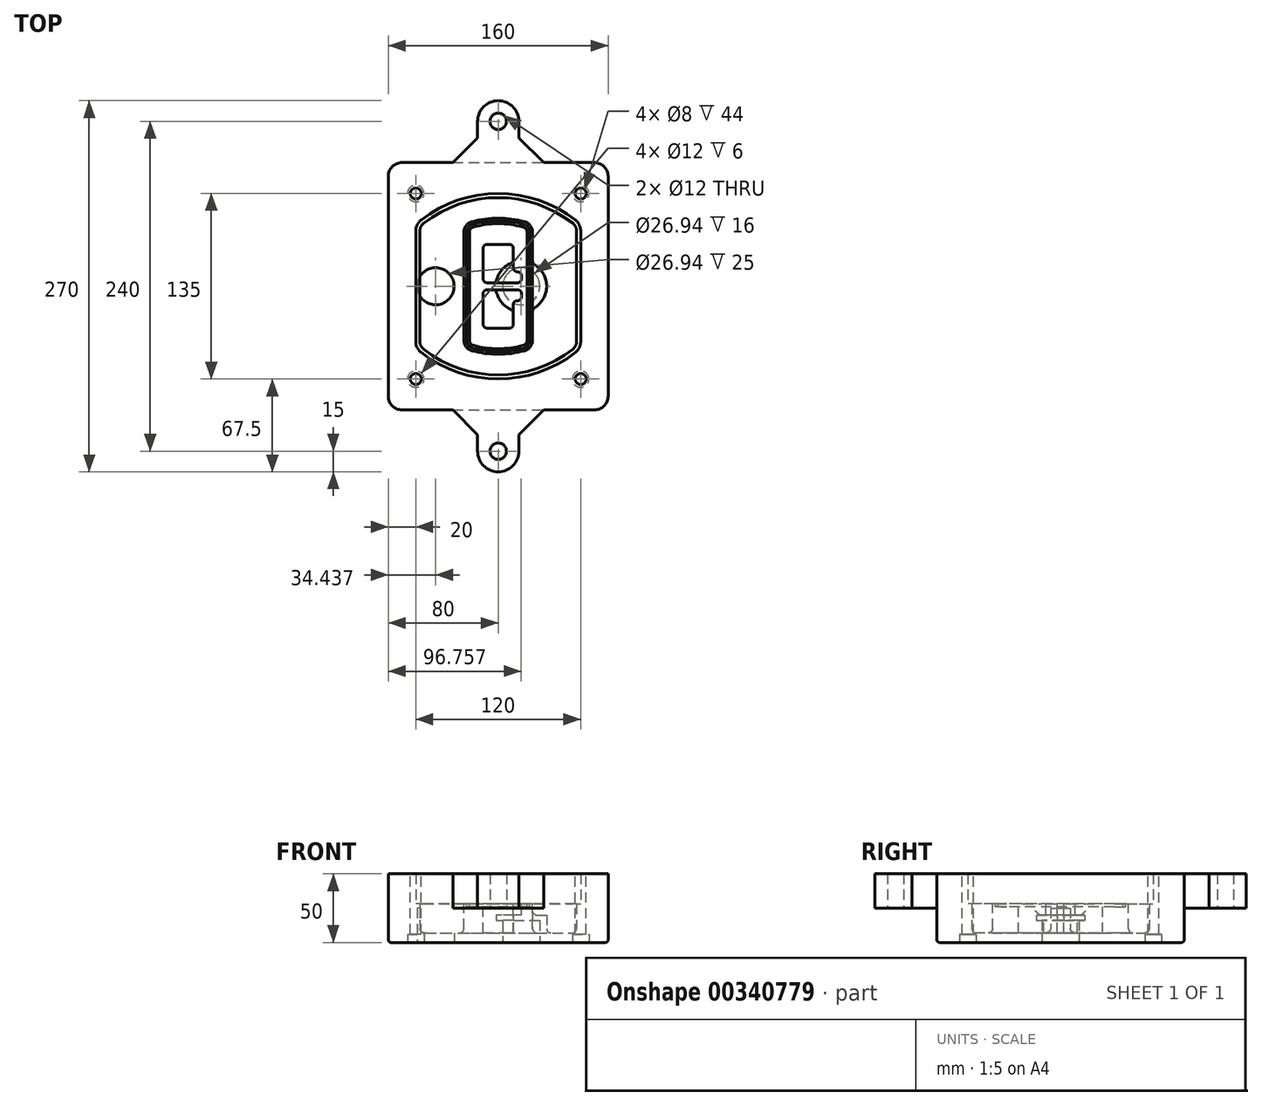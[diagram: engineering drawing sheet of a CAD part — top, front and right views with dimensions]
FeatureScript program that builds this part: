
annotation { "Feature Type Name" : "Feature", "Feature Type Description" : "" }
export const myFeature = defineFeature(function(context is Context, id is Id, definition is map)
    precondition{}
    {
        {
            var Q0;
            Q0=qCreatedBy(makeId("Top.planeOp"),FACE);
            var sketch = newSketch(context, id + "F0", { "sketchPlane" : qUnion([Q0])});
            skPoint(sketch, "E0.rect.middle", {"position": v(0, 0) * mm});
            skLineSegment(sketch, "E1.bottom", {"start": v(-70, -90) * mm, "end": v(70, -90) * mm});
            skLineSegment(sketch, "E1.top", {"start": v(-70, 90) * mm, "end": v(70, 90) * mm});
            skLineSegment(sketch, "E1.left", {"start": v(-80, -80) * mm, "end": v(-80, 80) * mm});
            skLineSegment(sketch, "E1.right", {"start": v(80, -80) * mm, "end": v(80, 80) * mm});
            skLineSegment(sketch, "E2", {"start": v(-80, 90) * mm, "end": v(80, -90) * mm, "construction": true});
            skLineSegment(sketch, "E3", {"start": v(80, 90) * mm, "end": v(-80, -90) * mm, "construction": true});
            skCircle(sketch, "E4", {"center": v(-60, 67.5) * mm, "radius": 4 * mm});
            skCircle(sketch, "E5", {"center": v(60, 67.5) * mm, "radius": 4 * mm});
            skCircle(sketch, "E6", {"center": v(60, -67.5) * mm, "radius": 4 * mm});
            skCircle(sketch, "E7", {"center": v(-60, -67.5) * mm, "radius": 4 * mm});
            skLineSegment(sketch, "E8", {"start": v(-60, 67.5) * mm, "end": v(60, 67.5) * mm, "construction": true});
            skLineSegment(sketch, "E9", {"start": v(60, 67.5) * mm, "end": v(60, -67.5) * mm, "construction": true});
            skLineSegment(sketch, "E10", {"start": v(60, -67.5) * mm, "end": v(-60, -67.5) * mm, "construction": true});
            skLineSegment(sketch, "E11", {"start": v(-60, -67.5) * mm, "end": v(-60, 67.5) * mm, "construction": true});
            skLineSegment(sketch, "E12", {"start": v(-60, 40.3) * mm, "end": v(-60, -40.3) * mm});
            skLineSegment(sketch, "E13", {"start": v(60, 40.3) * mm, "end": v(60, -40.3) * mm});
            skArc(sketch, "E14", {"start": v(56.15, 48.18) * mm, "mid": v(0, 67.5) * mm, "end": v(-56.15, 48.18) * mm});
            skArc(sketch, "E15", {"start": v(-56.15, -48.18) * mm, "mid": v(0, -67.5) * mm, "end": v(56.15, -48.18) * mm});
            skLineSegment(sketch, "E16", {"start": v(-60, 0) * mm, "end": v(60, 0) * mm, "construction": true});
            skPoint(sketch, "E17.visualSharp", {"position": v(-60, -45) * mm});
            skArc(sketch, "E17.filletArc", {"start": v(-60, -40.3) * mm, "mid": v(-58.99, -44.68) * mm, "end": v(-56.15, -48.18) * mm});
            skPoint(sketch, "E18.visualSharp", {"position": v(-60, 45) * mm});
            skArc(sketch, "E18.filletArc", {"start": v(-56.15, 48.18) * mm, "mid": v(-58.99, 44.68) * mm, "end": v(-60, 40.3) * mm});
            skPoint(sketch, "E19.visualSharp", {"position": v(60, 45) * mm});
            skArc(sketch, "E19.filletArc", {"start": v(60, 40.3) * mm, "mid": v(58.99, 44.68) * mm, "end": v(56.15, 48.18) * mm});
            skPoint(sketch, "E20.visualSharp", {"position": v(60, -45) * mm});
            skArc(sketch, "E20.filletArc", {"start": v(56.15, -48.18) * mm, "mid": v(58.99, -44.68) * mm, "end": v(60, -40.3) * mm});
            skPoint(sketch, "E21.visualSharp", {"position": v(-80, 90) * mm});
            skArc(sketch, "E21.filletArc", {"start": v(-70, 90) * mm, "mid": v(-77.07, 87.07) * mm, "end": v(-80, 80) * mm});
            skPoint(sketch, "E22.visualSharp", {"position": v(80, 90) * mm});
            skArc(sketch, "E22.filletArc", {"start": v(80, 80) * mm, "mid": v(77.07, 87.07) * mm, "end": v(70, 90) * mm});
            skPoint(sketch, "E23.visualSharp", {"position": v(80, -90) * mm});
            skArc(sketch, "E23.filletArc", {"start": v(70, -90) * mm, "mid": v(77.07, -87.07) * mm, "end": v(80, -80) * mm});
            skPoint(sketch, "E24.visualSharp", {"position": v(-80, -90) * mm});
            skArc(sketch, "E24.filletArc", {"start": v(-80, -80) * mm, "mid": v(-77.07, -87.07) * mm, "end": v(-70, -90) * mm});
            skArc(sketch, "E25.0", {"start": v(57, 40.3) * mm, "mid": v(56.3, 43.36) * mm, "end": v(54.3, 45.81) * mm});
            skLineSegment(sketch, "E25.1", {"start": v(57, 40.3) * mm, "end": v(57, -40.3) * mm});
            skArc(sketch, "E25.2", {"start": v(54.3, -45.81) * mm, "mid": v(56.3, -43.36) * mm, "end": v(57, -40.3) * mm});
            skArc(sketch, "E25.3", {"start": v(-54.3, -45.81) * mm, "mid": v(0, -64.5) * mm, "end": v(54.3, -45.81) * mm});
            skArc(sketch, "E25.4", {"start": v(-57, -40.3) * mm, "mid": v(-56.3, -43.36) * mm, "end": v(-54.3, -45.81) * mm});
            skArc(sketch, "E25.5", {"start": v(54.3, 45.81) * mm, "mid": v(0, 64.5) * mm, "end": v(-54.3, 45.81) * mm});
            skLineSegment(sketch, "E25.6", {"start": v(-57, 40.3) * mm, "end": v(-57, -40.3) * mm});
            skArc(sketch, "E25.7", {"start": v(-54.3, 45.81) * mm, "mid": v(-56.3, 43.36) * mm, "end": v(-57, 40.3) * mm});
            skArc(sketch, "E26.0", {"start": v(-58.62, 51.33) * mm, "mid": v(-62.58, 46.43) * mm, "end": v(-64, 40.3) * mm});
            skArc(sketch, "E26.1", {"start": v(58.62, 51.33) * mm, "mid": v(0, 71.5) * mm, "end": v(-58.62, 51.33) * mm});
            skArc(sketch, "E26.2", {"start": v(64, 40.3) * mm, "mid": v(62.58, 46.43) * mm, "end": v(58.62, 51.33) * mm});
            skLineSegment(sketch, "E26.3", {"start": v(64, 40.3) * mm, "end": v(64, -40.3) * mm});
            skArc(sketch, "E26.4", {"start": v(58.62, -51.33) * mm, "mid": v(62.58, -46.43) * mm, "end": v(64, -40.3) * mm});
            skLineSegment(sketch, "E26.5", {"start": v(-64, 40.3) * mm, "end": v(-64, -40.3) * mm});
            skArc(sketch, "E26.6", {"start": v(-58.62, -51.33) * mm, "mid": v(0, -71.5) * mm, "end": v(58.62, -51.33) * mm});
            skArc(sketch, "E26.7", {"start": v(-64, -40.3) * mm, "mid": v(-62.58, -46.43) * mm, "end": v(-58.62, -51.33) * mm});
            skSolve(sketch);
        }
        {
            var Q0;
            Q0=makeQuery(id+"F0.imprint","IMPRINT",FACE,{"disambiguationData":[TD([[makeQuery(id+"F0.imprint","IMPRINT",EDGE,{"derivedFrom":sQuery(id+"F0.wireOp",EDGE,"E1.bottom")}),1.0]])]});
            var Q1;
            Q1=makeQuery(id+"F0.imprint","IMPRINT",FACE,{"disambiguationData":[TD([[makeQuery(id+"F0.imprint","IMPRINT",EDGE,{"derivedFrom":sQuery(id+"F0.wireOp",EDGE,"E12")}),1.0]])]});
            var Q2;
            Q2=makeQuery(id+"F0.imprint","IMPRINT",FACE,{"disambiguationData":[TD([[makeQuery(id+"F0.imprint","IMPRINT",EDGE,{"derivedFrom":sQuery(id+"F0.wireOp",EDGE,"E25.0")}),1.0]])]});
            var Q3;
            Q3=makeQuery(id+"F0.imprint","IMPRINT",FACE,{"disambiguationData":[TD([[makeQuery(id+"F0.imprint","IMPRINT",EDGE,{"derivedFrom":sQuery(id+"F0.wireOp",EDGE,"E12")}),-1.0]])]});
            extrude(context, id + "F1", {"entities" : qUnion([Q0, Q1, Q2, Q3]), "oppositeDirection" : true, "depth" : 25 * mm});
        }
        {
            var Q0;
            Q0=makeQuery(id+"F0.imprint","IMPRINT",FACE,{"disambiguationData":[TD([[makeQuery(id+"F0.imprint","IMPRINT",EDGE,{"derivedFrom":sQuery(id+"F0.wireOp",EDGE,"E12")}),1.0]])]});
            extrude(context, id + "F2", {"entities" : qUnion([Q0]), "operationType" : NewBodyOperationType.ADD, "depth" : 3 * mm});
        }
        {
            var Q0;
            Q0=makeQuery(id+"F0.imprint","IMPRINT",FACE,{"disambiguationData":[TD([[makeQuery(id+"F0.imprint","IMPRINT",EDGE,{"derivedFrom":sQuery(id+"F0.wireOp",EDGE,"E25.0")}),1.0]])]});
            extrude(context, id + "F3", {"entities" : qUnion([Q0]), "operationType" : NewBodyOperationType.REMOVE, "oppositeDirection" : true, "depth" : 18 * mm});
        }
        {
            var Q0;
            Q0=makeQuery(id+"F2.opExtrude","CAP_FACE",FACE,{"disambiguationData":[OSD([sQuery(id+"F0.wireOp",EDGE,"E12"),sQuery(id+"F0.wireOp",EDGE,"E13"),sQuery(id+"F0.wireOp",EDGE,"E14"),sQuery(id+"F0.wireOp",EDGE,"E15"),sQuery(id+"F0.wireOp",EDGE,"E17.filletArc"),sQuery(id+"F0.wireOp",EDGE,"E18.filletArc"),sQuery(id+"F0.wireOp",EDGE,"E19.filletArc"),sQuery(id+"F0.wireOp",EDGE,"E20.filletArc"),sQuery(id+"F0.wireOp",EDGE,"E25.0"),sQuery(id+"F0.wireOp",EDGE,"E25.1"),sQuery(id+"F0.wireOp",EDGE,"E25.2"),sQuery(id+"F0.wireOp",EDGE,"E25.3"),sQuery(id+"F0.wireOp",EDGE,"E25.4"),sQuery(id+"F0.wireOp",EDGE,"E25.5"),sQuery(id+"F0.wireOp",EDGE,"E25.6"),sQuery(id+"F0.wireOp",EDGE,"E25.7")])],"isStart":false});
            var sketch = newSketch(context, id + "F4", { "sketchPlane" : qUnion([Q0])});
            skArc(sketch, "E27.0", {"start": v(-19.08, -46.97) * mm, "mid": v(0, -49.5) * mm, "end": v(19.08, -46.97) * mm});
            skArc(sketch, "E28.0", {"start": v(19.08, 46.97) * mm, "mid": v(0, 49.5) * mm, "end": v(-19.08, 46.97) * mm});
            skLineSegment(sketch, "E29", {"start": v(-25, 39.25) * mm, "end": v(-25, -39.25) * mm});
            skLineSegment(sketch, "E30", {"start": v(25, 39.25) * mm, "end": v(25, -39.25) * mm});
            skLineSegment(sketch, "E31", {"start": v(-25, 45.1) * mm, "end": v(25, 45.1) * mm, "construction": true});
            skLineSegment(sketch, "E32", {"start": v(-25, -45.1) * mm, "end": v(25, -45.1) * mm, "construction": true});
            skPoint(sketch, "E33.visualSharp", {"position": v(-25, 45.1) * mm});
            skArc(sketch, "E33.filletArc", {"start": v(-19.08, 46.97) * mm, "mid": v(-23.35, 44.11) * mm, "end": v(-25, 39.25) * mm});
            skPoint(sketch, "E34.visualSharp", {"position": v(25, 45.1) * mm});
            skArc(sketch, "E34.filletArc", {"start": v(25, 39.25) * mm, "mid": v(23.35, 44.11) * mm, "end": v(19.08, 46.97) * mm});
            skPoint(sketch, "E35.visualSharp", {"position": v(25, -45.1) * mm});
            skArc(sketch, "E35.filletArc", {"start": v(19.08, -46.97) * mm, "mid": v(23.35, -44.11) * mm, "end": v(25, -39.25) * mm});
            skPoint(sketch, "E36.visualSharp", {"position": v(-25, -45.1) * mm});
            skArc(sketch, "E36.filletArc", {"start": v(-25, -39.25) * mm, "mid": v(-23.35, -44.11) * mm, "end": v(-19.08, -46.97) * mm});
            skArc(sketch, "E37.0", {"start": v(54.3, 45.81) * mm, "mid": v(0, 64.5) * mm, "end": v(-54.3, 45.81) * mm});
            skArc(sketch, "E37.1", {"start": v(-54.3, 45.81) * mm, "mid": v(-56.3, 43.36) * mm, "end": v(-57, 40.3) * mm});
            skLineSegment(sketch, "E37.2", {"start": v(-57, 40.3) * mm, "end": v(-57, -40.3) * mm});
            skArc(sketch, "E37.3", {"start": v(-57, -40.3) * mm, "mid": v(-56.3, -43.36) * mm, "end": v(-54.3, -45.81) * mm});
            skArc(sketch, "E37.4", {"start": v(-54.3, -45.81) * mm, "mid": v(0, -64.5) * mm, "end": v(54.3, -45.81) * mm});
            skArc(sketch, "E37.5", {"start": v(54.3, -45.81) * mm, "mid": v(56.3, -43.36) * mm, "end": v(57, -40.3) * mm});
            skLineSegment(sketch, "E37.6", {"start": v(57, 40.3) * mm, "end": v(57, -40.3) * mm});
            skArc(sketch, "E37.7", {"start": v(57, 40.3) * mm, "mid": v(56.3, 43.36) * mm, "end": v(54.3, 45.81) * mm});
            skLineSegment(sketch, "E38.0", {"start": v(23, 39.25) * mm, "end": v(23, -39.25) * mm});
            skArc(sketch, "E38.1", {"start": v(18.56, -45.04) * mm, "mid": v(21.76, -42.9) * mm, "end": v(23, -39.25) * mm});
            skArc(sketch, "E38.2", {"start": v(-18.56, -45.04) * mm, "mid": v(0, -47.5) * mm, "end": v(18.56, -45.04) * mm});
            skArc(sketch, "E38.3", {"start": v(-23, -39.25) * mm, "mid": v(-21.76, -42.9) * mm, "end": v(-18.56, -45.04) * mm});
            skLineSegment(sketch, "E38.4", {"start": v(-23, 39.25) * mm, "end": v(-23, -39.25) * mm});
            skArc(sketch, "E38.5", {"start": v(23, 39.25) * mm, "mid": v(21.76, 42.9) * mm, "end": v(18.56, 45.04) * mm});
            skArc(sketch, "E38.6", {"start": v(-18.56, 45.04) * mm, "mid": v(-21.76, 42.9) * mm, "end": v(-23, 39.25) * mm});
            skArc(sketch, "E38.7", {"start": v(18.56, 45.04) * mm, "mid": v(0, 47.5) * mm, "end": v(-18.56, 45.04) * mm});
            skArc(sketch, "E39.0", {"start": v(21, 39.25) * mm, "mid": v(20.18, 41.68) * mm, "end": v(18.04, 43.1) * mm});
            skLineSegment(sketch, "E39.1", {"start": v(21, 39.25) * mm, "end": v(21, -39.25) * mm});
            skArc(sketch, "E39.2", {"start": v(18.04, -43.1) * mm, "mid": v(20.18, -41.68) * mm, "end": v(21, -39.25) * mm});
            skArc(sketch, "E39.3", {"start": v(-18.04, -43.1) * mm, "mid": v(0, -45.5) * mm, "end": v(18.04, -43.1) * mm});
            skArc(sketch, "E39.4", {"start": v(-21, -39.25) * mm, "mid": v(-20.18, -41.68) * mm, "end": v(-18.04, -43.1) * mm});
            skArc(sketch, "E39.5", {"start": v(18.04, 43.1) * mm, "mid": v(0, 45.5) * mm, "end": v(-18.04, 43.1) * mm});
            skLineSegment(sketch, "E39.6", {"start": v(-21, 39.25) * mm, "end": v(-21, -39.25) * mm});
            skArc(sketch, "E39.7", {"start": v(-18.04, 43.1) * mm, "mid": v(-20.18, 41.68) * mm, "end": v(-21, 39.25) * mm});
            skLineSegment(sketch, "E40", {"start": v(-25, 0) * mm, "end": v(25, 0) * mm, "construction": true});
            skLineSegment(sketch, "E41", {"start": v(-11, 5.5) * mm, "end": v(-11, 27.5) * mm});
            skLineSegment(sketch, "E42", {"start": v(-8, 30.5) * mm, "end": v(8, 30.5) * mm});
            skLineSegment(sketch, "E43", {"start": v(11, 27.5) * mm, "end": v(11, 13.5) * mm});
            skLineSegment(sketch, "E44", {"start": v(14, 10.5) * mm, "end": v(14, 10.5) * mm});
            skLineSegment(sketch, "E45", {"start": v(17, 7.5) * mm, "end": v(17, 5.5) * mm});
            skLineSegment(sketch, "E46", {"start": v(14, 2.5) * mm, "end": v(-8, 2.5) * mm});
            skPoint(sketch, "E47.visualSharp", {"position": v(-11, 30.5) * mm});
            skArc(sketch, "E47.filletArc", {"start": v(-8, 30.5) * mm, "mid": v(-10.12, 29.62) * mm, "end": v(-11, 27.5) * mm});
            skPoint(sketch, "E48.visualSharp", {"position": v(11, 30.5) * mm});
            skArc(sketch, "E48.filletArc", {"start": v(11, 27.5) * mm, "mid": v(10.12, 29.62) * mm, "end": v(8, 30.5) * mm});
            skPoint(sketch, "E49.visualSharp", {"position": v(11, 10.5) * mm});
            skArc(sketch, "E49.filletArc", {"start": v(11, 13.5) * mm, "mid": v(11.88, 11.38) * mm, "end": v(14, 10.5) * mm});
            skPoint(sketch, "E50.visualSharp", {"position": v(17, 10.5) * mm});
            skArc(sketch, "E50.filletArc", {"start": v(17, 7.5) * mm, "mid": v(16.12, 9.62) * mm, "end": v(14, 10.5) * mm});
            skPoint(sketch, "E51.visualSharp", {"position": v(17, 2.5) * mm});
            skArc(sketch, "E51.filletArc", {"start": v(14, 2.5) * mm, "mid": v(16.12, 3.38) * mm, "end": v(17, 5.5) * mm});
            skPoint(sketch, "E52.visualSharp", {"position": v(-11, 2.5) * mm});
            skArc(sketch, "E52.filletArc", {"start": v(-11, 5.5) * mm, "mid": v(-10.12, 3.38) * mm, "end": v(-8, 2.5) * mm});
            skLineSegment(sketch, "E53.0.MirrorCS", {"start": v(14, -2.5) * mm, "end": v(-8, -2.5) * mm});
            skArc(sketch, "E54.0.MirrorCS", {"start": v(-11, -5.5) * mm, "mid": v(-10.12, -3.38) * mm, "end": v(-8, -2.5) * mm});
            skLineSegment(sketch, "E55.0.MirrorCS", {"start": v(-11, -5.5) * mm, "end": v(-11, -27.5) * mm});
            skArc(sketch, "E56.0.MirrorCS", {"start": v(-8, -30.5) * mm, "mid": v(-10.12, -29.62) * mm, "end": v(-11, -27.5) * mm});
            skLineSegment(sketch, "E57.0.MirrorCS", {"start": v(-8, -30.5) * mm, "end": v(8, -30.5) * mm});
            skArc(sketch, "E58.0.MirrorCS", {"start": v(11, -27.5) * mm, "mid": v(10.12, -29.62) * mm, "end": v(8, -30.5) * mm});
            skLineSegment(sketch, "E59.0.MirrorCS", {"start": v(11, -27.5) * mm, "end": v(11, -13.5) * mm});
            skArc(sketch, "E60.0.MirrorCS", {"start": v(11, -13.5) * mm, "mid": v(11.88, -11.38) * mm, "end": v(14, -10.5) * mm});
            skArc(sketch, "E61.0.MirrorCS", {"start": v(17, -7.5) * mm, "mid": v(16.12, -9.62) * mm, "end": v(14, -10.5) * mm});
            skLineSegment(sketch, "E62.0.MirrorCS", {"start": v(17, -7.5) * mm, "end": v(17, -5.5) * mm});
            skArc(sketch, "E63.0.MirrorCS", {"start": v(14, -2.5) * mm, "mid": v(16.12, -3.38) * mm, "end": v(17, -5.5) * mm});
            skSolve(sketch);
        }
        {
            var Q0;
            Q0=makeQuery(id+"F4.imprint","IMPRINT",FACE,{"disambiguationData":[TD([[makeQuery(id+"F4.imprint","IMPRINT",EDGE,{"derivedFrom":sQuery(id+"F4.wireOp",EDGE,"E27.0")}),1.0]])]});
            var Q1;
            Q1=makeQuery(id+"F4.imprint","IMPRINT",FACE,{"disambiguationData":[TD([[makeQuery(id+"F4.imprint","IMPRINT",EDGE,{"derivedFrom":sQuery(id+"F4.wireOp",EDGE,"E38.0")}),-1.0]])]});
            var Q2;
            Q2=makeQuery(id+"F4.imprint","IMPRINT",FACE,{"disambiguationData":[TD([[makeQuery(id+"F4.imprint","IMPRINT",EDGE,{"derivedFrom":sQuery(id+"F4.wireOp",EDGE,"E39.0")}),1.0]])]});
            extrude(context, id + "F5", {"entities" : qUnion([Q0, Q1, Q2]), "operationType" : NewBodyOperationType.ADD, "endBound" : BoundingType.UP_TO_NEXT, "oppositeDirection" : true, "depth" : 25 * mm});
        }
        {
            var Q0;
            Q0=makeQuery(id+"F4.imprint","IMPRINT",FACE,{"disambiguationData":[TD([[makeQuery(id+"F4.imprint","IMPRINT",EDGE,{"derivedFrom":sQuery(id+"F4.wireOp",EDGE,"E38.0")}),-1.0]])]});
            extrude(context, id + "F6", {"entities" : qUnion([Q0]), "operationType" : NewBodyOperationType.REMOVE, "oppositeDirection" : true, "depth" : 2 * mm});
        }
        {
            var Q0;
            Q0=makeQuery(id+"F1.opExtrude","CAP_FACE",FACE,{"disambiguationData":[OSD([sQuery(id+"F0.wireOp",EDGE,"E1.bottom"),sQuery(id+"F0.wireOp",EDGE,"E1.top"),sQuery(id+"F0.wireOp",EDGE,"E1.left"),sQuery(id+"F0.wireOp",EDGE,"E1.right"),sQuery(id+"F0.wireOp",EDGE,"E4"),sQuery(id+"F0.wireOp",EDGE,"E5"),sQuery(id+"F0.wireOp",EDGE,"E6"),sQuery(id+"F0.wireOp",EDGE,"E7"),sQuery(id+"F0.wireOp",EDGE,"E21.filletArc"),sQuery(id+"F0.wireOp",EDGE,"E22.filletArc"),sQuery(id+"F0.wireOp",EDGE,"E23.filletArc"),sQuery(id+"F0.wireOp",EDGE,"E24.filletArc")])],"isStart":false});
            var sketch = newSketch(context, id + "F7", { "sketchPlane" : qUnion([Q0])});
            skCircle(sketch, "E64", {"center": v(16.76, 0) * mm, "radius": 13.47 * mm});
            skCircle(sketch, "E65", {"center": v(-45.56, 0) * mm, "radius": 13.47 * mm});
            skLineSegment(sketch, "E66", {"start": v(80, 0) * mm, "end": v(-80, 0) * mm});
            skCircle(sketch, "E67", {"center": v(16.76, 0) * mm, "radius": 18.47 * mm});
            skCircle(sketch, "E68", {"center": v(60, -67.5) * mm, "radius": 6 * mm});
            skCircle(sketch, "E69", {"center": v(-60, -67.5) * mm, "radius": 6 * mm});
            skCircle(sketch, "E70", {"center": v(-60, 67.5) * mm, "radius": 6 * mm});
            skCircle(sketch, "E71", {"center": v(60, 67.5) * mm, "radius": 6 * mm});
            skSolve(sketch);
        }
        {
            var Q0;
            {var subQ1=sQuery(id+"F7.wireOp",EDGE,"E66");var subQ4=sQuery(id+"F7.wireOp",EDGE,"E64");var subQ6=makeQuery(id+"F7.imprint","INTERSECT",VERTEX,{"disambiguationData":[OD(0.0)],"derivedFrom":[subQ4,subQ1]});Q0=makeQuery(id+"F7.imprint","IMPRINT",FACE,{"disambiguationData":[TD([[makeQuery(id+"F7.imprint","IMPRINT",EDGE,{"disambiguationData":[TD([[subQ6,-1.0]])],"derivedFrom":subQ4}),-1.0]])]});}
            var Q1;
            {var subQ0=sQuery(id+"F7.wireOp",EDGE,"E66");var subQ1=sQuery(id+"F7.wireOp",EDGE,"E64");var subQ3=makeQuery(id+"F7.imprint","INTERSECT",VERTEX,{"disambiguationData":[OD(0.0)],"derivedFrom":[subQ1,subQ0]});Q1=makeQuery(id+"F7.imprint","IMPRINT",FACE,{"disambiguationData":[TD([[makeQuery(id+"F7.imprint","IMPRINT",EDGE,{"disambiguationData":[TD([[subQ3,-1.0]])],"derivedFrom":subQ1}),1.0]])]});}
            var Q2;
            {var subQ0=sQuery(id+"F7.wireOp",EDGE,"E66");var subQ1=sQuery(id+"F7.wireOp",EDGE,"E64");var subQ3=makeQuery(id+"F7.imprint","INTERSECT",VERTEX,{"disambiguationData":[OD(0.0)],"derivedFrom":[subQ1,subQ0]});Q2=makeQuery(id+"F7.imprint","IMPRINT",FACE,{"disambiguationData":[TD([[makeQuery(id+"F7.imprint","IMPRINT",EDGE,{"disambiguationData":[TD([[subQ3,1.0]])],"derivedFrom":subQ1}),1.0]])]});}
            var Q3;
            {var subQ1=sQuery(id+"F7.wireOp",EDGE,"E66");var subQ4=sQuery(id+"F7.wireOp",EDGE,"E64");var subQ6=makeQuery(id+"F7.imprint","INTERSECT",VERTEX,{"disambiguationData":[OD(0.0)],"derivedFrom":[subQ4,subQ1]});Q3=makeQuery(id+"F7.imprint","IMPRINT",FACE,{"disambiguationData":[TD([[makeQuery(id+"F7.imprint","IMPRINT",EDGE,{"disambiguationData":[TD([[subQ6,1.0]])],"derivedFrom":subQ4}),-1.0]])]});}
            extrude(context, id + "F8", {"entities" : qUnion([Q0, Q1, Q2, Q3]), "operationType" : NewBodyOperationType.ADD, "oppositeDirection" : true, "depth" : 20 * mm});
        }
        {
            var Q0;
            {var subQ0=sQuery(id+"F7.wireOp",EDGE,"E66");var subQ1=sQuery(id+"F7.wireOp",EDGE,"E64");var subQ3=makeQuery(id+"F7.imprint","INTERSECT",VERTEX,{"disambiguationData":[OD(0.0)],"derivedFrom":[subQ1,subQ0]});Q0=makeQuery(id+"F7.imprint","IMPRINT",FACE,{"disambiguationData":[TD([[makeQuery(id+"F7.imprint","IMPRINT",EDGE,{"disambiguationData":[TD([[subQ3,-1.0]])],"derivedFrom":subQ1}),1.0]])]});}
            var Q1;
            {var subQ0=sQuery(id+"F7.wireOp",EDGE,"E66");var subQ1=sQuery(id+"F7.wireOp",EDGE,"E64");var subQ3=makeQuery(id+"F7.imprint","INTERSECT",VERTEX,{"disambiguationData":[OD(0.0)],"derivedFrom":[subQ1,subQ0]});Q1=makeQuery(id+"F7.imprint","IMPRINT",FACE,{"disambiguationData":[TD([[makeQuery(id+"F7.imprint","IMPRINT",EDGE,{"disambiguationData":[TD([[subQ3,1.0]])],"derivedFrom":subQ1}),1.0]])]});}
            extrude(context, id + "F9", {"entities" : qUnion([Q0, Q1]), "operationType" : NewBodyOperationType.REMOVE, "oppositeDirection" : true, "depth" : 16 * mm});
        }
        {
            var Q0;
            {var subQ0=sQuery(id+"F7.wireOp",EDGE,"E66");var subQ1=sQuery(id+"F7.wireOp",EDGE,"E65");var subQ3=makeQuery(id+"F7.imprint","INTERSECT",VERTEX,{"disambiguationData":[OD(0.0)],"derivedFrom":[subQ1,subQ0]});Q0=makeQuery(id+"F7.imprint","IMPRINT",FACE,{"disambiguationData":[TD([[makeQuery(id+"F7.imprint","IMPRINT",EDGE,{"disambiguationData":[TD([[subQ3,-1.0]])],"derivedFrom":subQ1}),1.0]])]});}
            var Q1;
            {var subQ0=sQuery(id+"F7.wireOp",EDGE,"E66");var subQ1=sQuery(id+"F7.wireOp",EDGE,"E65");var subQ3=makeQuery(id+"F7.imprint","INTERSECT",VERTEX,{"disambiguationData":[OD(0.0)],"derivedFrom":[subQ1,subQ0]});Q1=makeQuery(id+"F7.imprint","IMPRINT",FACE,{"disambiguationData":[TD([[makeQuery(id+"F7.imprint","IMPRINT",EDGE,{"disambiguationData":[TD([[subQ3,1.0]])],"derivedFrom":subQ1}),1.0]])]});}
            extrude(context, id + "F10", {"entities" : qUnion([Q0, Q1]), "operationType" : NewBodyOperationType.REMOVE, "oppositeDirection" : true, "depth" : 25 * mm});
        }
        {
            var Q0;
            Q0=makeQuery(id+"F7.imprint","IMPRINT",FACE,{"disambiguationData":[TD([[makeQuery(id+"F7.imprint","IMPRINT",EDGE,{"derivedFrom":sQuery(id+"F7.wireOp",EDGE,"E68")}),1.0]])]});
            var Q1;
            Q1=makeQuery(id+"F7.imprint","IMPRINT",FACE,{"disambiguationData":[TD([[makeQuery(id+"F7.imprint","IMPRINT",EDGE,{"derivedFrom":makeQuery(id+"F1.opExtrude","CAP_EDGE",EDGE,{"disambiguationData":[OSD([sQuery(id+"F0.wireOp",EDGE,"E5")])],"isStart":false})}),-1.0]])]});
            var Q2;
            Q2=makeQuery(id+"F7.imprint","IMPRINT",FACE,{"disambiguationData":[TD([[makeQuery(id+"F7.imprint","IMPRINT",EDGE,{"derivedFrom":sQuery(id+"F7.wireOp",EDGE,"E69")}),1.0]])]});
            var Q3;
            Q3=makeQuery(id+"F7.imprint","IMPRINT",FACE,{"disambiguationData":[TD([[makeQuery(id+"F7.imprint","IMPRINT",EDGE,{"derivedFrom":makeQuery(id+"F1.opExtrude","CAP_EDGE",EDGE,{"disambiguationData":[OSD([sQuery(id+"F0.wireOp",EDGE,"E4")])],"isStart":false})}),-1.0]])]});
            var Q4;
            Q4=makeQuery(id+"F7.imprint","IMPRINT",FACE,{"disambiguationData":[TD([[makeQuery(id+"F7.imprint","IMPRINT",EDGE,{"derivedFrom":sQuery(id+"F7.wireOp",EDGE,"E70")}),1.0]])]});
            var Q5;
            Q5=makeQuery(id+"F7.imprint","IMPRINT",FACE,{"disambiguationData":[TD([[makeQuery(id+"F7.imprint","IMPRINT",EDGE,{"derivedFrom":makeQuery(id+"F1.opExtrude","CAP_EDGE",EDGE,{"disambiguationData":[OSD([sQuery(id+"F0.wireOp",EDGE,"E7")])],"isStart":false})}),-1.0]])]});
            var Q6;
            Q6=makeQuery(id+"F7.imprint","IMPRINT",FACE,{"disambiguationData":[TD([[makeQuery(id+"F7.imprint","IMPRINT",EDGE,{"derivedFrom":sQuery(id+"F7.wireOp",EDGE,"E71")}),1.0]])]});
            var Q7;
            Q7=makeQuery(id+"F7.imprint","IMPRINT",FACE,{"disambiguationData":[TD([[makeQuery(id+"F7.imprint","IMPRINT",EDGE,{"derivedFrom":makeQuery(id+"F1.opExtrude","CAP_EDGE",EDGE,{"disambiguationData":[OSD([sQuery(id+"F0.wireOp",EDGE,"E6")])],"isStart":false})}),-1.0]])]});
            extrude(context, id + "F11", {"entities" : qUnion([Q0, Q1, Q2, Q3, Q4, Q5, Q6, Q7]), "operationType" : NewBodyOperationType.REMOVE, "oppositeDirection" : true, "depth" : 6 * mm});
        }
        {
            var Q0;
            Q0=makeQuery(id+"F9.boolean.opBoolean","COPY",FACE,{"derivedFrom":makeQuery(id+"F9.opExtrude","CAP_FACE",FACE,{"disambiguationData":[OSD([sQuery(id+"F7.wireOp",EDGE,"E64")])],"isStart":false})});
            var sketch = newSketch(context, id + "F12", { "sketchPlane" : qUnion([Q0])});
            skArc(sketch, "E72.0", {"start": v(11, 17.55) * mm, "mid": v(2.57, 11.82) * mm, "end": v(-1.54, 2.5) * mm});
            skArc(sketch, "E72.1", {"start": v(-1.54, -2.5) * mm, "mid": v(2.57, -11.82) * mm, "end": v(11, -17.55) * mm});
            skLineSegment(sketch, "E73", {"start": v(-1.54, -2.5) * mm, "end": v(14, -2.5) * mm});
            skLineSegment(sketch, "E74.0", {"start": v(14, 2.5) * mm, "end": v(-1.54, 2.5) * mm});
            skArc(sketch, "E74.1", {"start": v(14, 2.5) * mm, "mid": v(16.12, 3.38) * mm, "end": v(17, 5.5) * mm});
            skLineSegment(sketch, "E74.2", {"start": v(17, 7.5) * mm, "end": v(17, 5.5) * mm});
            skArc(sketch, "E74.3", {"start": v(17, 7.5) * mm, "mid": v(16.12, 9.62) * mm, "end": v(14, 10.5) * mm});
            skArc(sketch, "E74.4", {"start": v(11, 13.5) * mm, "mid": v(11.88, 11.38) * mm, "end": v(14, 10.5) * mm});
            skLineSegment(sketch, "E74.5", {"start": v(11, 17.55) * mm, "end": v(11, 13.5) * mm});
            skLineSegment(sketch, "E74.7", {"start": v(14, -2.5) * mm, "end": v(-1.54, -2.5) * mm});
            skArc(sketch, "E74.8", {"start": v(14, -2.5) * mm, "mid": v(16.12, -3.38) * mm, "end": v(17, -5.5) * mm});
            skLineSegment(sketch, "E74.9", {"start": v(17, -7.5) * mm, "end": v(17, -5.5) * mm});
            skArc(sketch, "E74.10", {"start": v(17, -7.5) * mm, "mid": v(16.12, -9.62) * mm, "end": v(14, -10.5) * mm});
            skArc(sketch, "E74.11", {"start": v(11, -13.5) * mm, "mid": v(11.88, -11.38) * mm, "end": v(14, -10.5) * mm});
            skLineSegment(sketch, "E74.12", {"start": v(11, -17.55) * mm, "end": v(11, -13.5) * mm});
            skPoint(sketch, "E75.orphan", {"position": v(11, -27.5) * mm});
            skPoint(sketch, "E76.orphan", {"position": v(-8, -2.5) * mm});
            skPoint(sketch, "E77.orphan", {"position": v(-8, 2.5) * mm});
            skPoint(sketch, "E78.orphan", {"position": v(11, 27.5) * mm});
            skSolve(sketch);
        }
        {
            var Q0;
            {var subQ7=sQuery(id+"F12.wireOp",EDGE,"E72.0");var subQ14=sQuery(id+"F12.wireOp",EDGE,"E72.1");var subQ16=sQuery(id+"F12.wireOp",EDGE,"E74.1");var subQ18=sQuery(id+"F12.wireOp",EDGE,"E74.8");Q0=qUnion([makeQuery(id+"F12.imprint","IMPRINT",FACE,{"disambiguationData":[TD([[makeQuery(id+"F12.imprint","IMPRINT",EDGE,{"derivedFrom":subQ7}),1.0]])]}),makeQuery(id+"F12.imprint","IMPRINT",FACE,{"disambiguationData":[TD([[makeQuery(id+"F12.imprint","IMPRINT",EDGE,{"derivedFrom":subQ14}),1.0]])]}),makeQuery(id+"F12.imprint","IMPRINT",FACE,{"disambiguationData":[TD([[makeQuery(id+"F12.imprint","IMPRINT",EDGE,{"derivedFrom":subQ16}),1.0]])]}),makeQuery(id+"F12.imprint","IMPRINT",FACE,{"disambiguationData":[TD([[makeQuery(id+"F12.imprint","IMPRINT",EDGE,{"derivedFrom":subQ18}),-1.0]])]})]);}
            var Q1;
            Q1=makeQuery(id+"F5.boolean.opBoolean","SPLIT",FACE,{"disambiguationData":[TD([makeQuery(id+"F5.opExtrude","SWEPT_FACE",FACE,{"disambiguationData":[OSD([sQuery(id+"F4.wireOp",EDGE,"E41")])]})])],"derivedFrom":makeQuery(id+"F3.boolean.opBoolean","COPY",FACE,{"derivedFrom":makeQuery(id+"F3.opExtrude","CAP_FACE",FACE,{"disambiguationData":[OSD([sQuery(id+"F0.wireOp",EDGE,"E25.0"),sQuery(id+"F0.wireOp",EDGE,"E25.1"),sQuery(id+"F0.wireOp",EDGE,"E25.2"),sQuery(id+"F0.wireOp",EDGE,"E25.3"),sQuery(id+"F0.wireOp",EDGE,"E25.4"),sQuery(id+"F0.wireOp",EDGE,"E25.5"),sQuery(id+"F0.wireOp",EDGE,"E25.6"),sQuery(id+"F0.wireOp",EDGE,"E25.7")])],"isStart":false})})});
            extrude(context, id + "F13", {"entities" : qUnion([Q0]), "operationType" : NewBodyOperationType.REMOVE, "endBound" : BoundingType.UP_TO_SURFACE, "endBoundEntityFace" : qUnion([Q1]), "depth" : 25 * mm});
        }
        {
            var Q0;
            Q0=makeQuery(id+"F3.boolean.opBoolean","COPY",EDGE,{"derivedFrom":makeQuery(id+"F3.opExtrude","CAP_EDGE",EDGE,{"disambiguationData":[OSD([sQuery(id+"F0.wireOp",EDGE,"E25.6")])],"isStart":false})});
            var Q1;
            Q1=makeQuery(id+"F8.boolean.opBoolean","INTERSECT",EDGE,{"derivedFrom":[makeQuery(id+"F5.opExtrude","SWEPT_FACE",FACE,{"disambiguationData":[OSD([sQuery(id+"F4.wireOp",EDGE,"E30")])]}),makeQuery(id+"F8.opExtrude","CAP_FACE",FACE,{"disambiguationData":[OSD([sQuery(id+"F7.wireOp",EDGE,"E67")])],"isStart":false})]});
            var Q2;
            Q2=makeQuery(id+"F8.boolean.opBoolean","INTERSECT",EDGE,{"disambiguationData":[OD(1.0)],"derivedFrom":[makeQuery(id+"F5.opExtrude","SWEPT_FACE",FACE,{"disambiguationData":[OSD([sQuery(id+"F4.wireOp",EDGE,"E30")])]}),makeQuery(id+"F8.opExtrude","SWEPT_FACE",FACE,{"disambiguationData":[OSD([sQuery(id+"F7.wireOp",EDGE,"E67")])]})]});
            var Q3;
            {var subQ0=sQuery(id+"F4.wireOp",EDGE,"E30");Q3=makeQuery(id+"F8.boolean.opBoolean","SPLIT",EDGE,{"disambiguationData":[TD([makeQuery(id+"F5.opExtrude","SWEPT_FACE",FACE,{"disambiguationData":[OSD([sQuery(id+"F4.wireOp",EDGE,"E35.filletArc")])]})])],"derivedFrom":makeQuery(id+"F5.opExtrude","CAP_EDGE",EDGE,{"disambiguationData":[OSD([subQ0])],"isStart":false})});}
            var Q4;
            {var subQ0=sQuery(id+"F0.wireOp",EDGE,"E25.7");var subQ1=sQuery(id+"F0.wireOp",EDGE,"E25.1");var subQ2=sQuery(id+"F0.wireOp",EDGE,"E25.6");var subQ3=sQuery(id+"F0.wireOp",EDGE,"E25.5");var subQ4=sQuery(id+"F0.wireOp",EDGE,"E25.4");var subQ5=sQuery(id+"F0.wireOp",EDGE,"E25.0");var subQ6=sQuery(id+"F0.wireOp",EDGE,"E25.2");var subQ7=sQuery(id+"F0.wireOp",EDGE,"E25.3");Q4=makeQuery(id+"F8.boolean.opBoolean","INTERSECT",EDGE,{"derivedFrom":[makeQuery(id+"F5.boolean.opBoolean","SPLIT",FACE,{"disambiguationData":[TD([makeQuery(id+"F2.opExtrude","SWEPT_FACE",FACE,{"disambiguationData":[OSD([subQ5])]})])],"derivedFrom":makeQuery(id+"F3.boolean.opBoolean","COPY",FACE,{"derivedFrom":makeQuery(id+"F3.opExtrude","CAP_FACE",FACE,{"disambiguationData":[OSD([subQ5,subQ1,subQ6,subQ7,subQ4,subQ3,subQ2,subQ0])],"isStart":false})})}),makeQuery(id+"F8.opExtrude","SWEPT_FACE",FACE,{"disambiguationData":[OSD([sQuery(id+"F7.wireOp",EDGE,"E67")])]})]});}
            var Q5;
            Q5=makeQuery(id+"F8.boolean.opBoolean","INTERSECT",EDGE,{"disambiguationData":[OD(0.0)],"derivedFrom":[makeQuery(id+"F5.opExtrude","SWEPT_FACE",FACE,{"disambiguationData":[OSD([sQuery(id+"F4.wireOp",EDGE,"E30")])]}),makeQuery(id+"F8.opExtrude","SWEPT_FACE",FACE,{"disambiguationData":[OSD([sQuery(id+"F7.wireOp",EDGE,"E67")])]})]});
            fillet(context, id + "F14", {"entities" : qUnion([Q0, Q1, Q2, Q3, Q4, Q5]), "radius" : 3 * mm, "tangentPropagation" : true, "allowEdgeOverflow" : false});
        }
        {
            var Q0;
            Q0=makeQuery(id+"F1.opExtrude","CAP_EDGE",EDGE,{"disambiguationData":[OSD([sQuery(id+"F0.wireOp",EDGE,"E1.bottom")])],"isStart":false});
            fillet(context, id + "F15", {"entities" : qUnion([Q0]), "radius" : 2 * mm, "tangentPropagation" : true, "allowEdgeOverflow" : false});
        }
        {
            var Q0;
            {var subQ0=sQuery(id+"F0.wireOp",EDGE,"E21.filletArc");var subQ1=sQuery(id+"F0.wireOp",EDGE,"E7");var subQ2=sQuery(id+"F0.wireOp",EDGE,"E6");var subQ3=sQuery(id+"F0.wireOp",EDGE,"E5");var subQ4=sQuery(id+"F0.wireOp",EDGE,"E4");var subQ5=sQuery(id+"F0.wireOp",EDGE,"E22.filletArc");var subQ6=sQuery(id+"F0.wireOp",EDGE,"E1.bottom");var subQ7=sQuery(id+"F0.wireOp",EDGE,"E1.right");var subQ8=sQuery(id+"F0.wireOp",EDGE,"E1.top");var subQ9=sQuery(id+"F0.wireOp",EDGE,"E1.left");var subQ10=sQuery(id+"F0.wireOp",EDGE,"E23.filletArc");var subQ11=sQuery(id+"F0.wireOp",EDGE,"E24.filletArc");Q0=makeQuery(id+"F2.boolean.opBoolean","SPLIT",FACE,{"disambiguationData":[TD([makeQuery(id+"F1.opExtrude","SWEPT_FACE",FACE,{"disambiguationData":[OSD([subQ6])]})])],"derivedFrom":makeQuery(id+"F1.opExtrude","CAP_FACE",FACE,{"disambiguationData":[OSD([subQ6,subQ8,subQ9,subQ7,subQ4,subQ3,subQ2,subQ1,subQ0,subQ5,subQ10,subQ11])],"isStart":true})});}
            var sketch = newSketch(context, id + "F16", { "sketchPlane" : qUnion([Q0])});
            skLineSegment(sketch, "E79.0", {"start": v(-80, -80) * mm, "end": v(-80, 80) * mm});
            skArc(sketch, "E79.1", {"start": v(-70, 90) * mm, "mid": v(-77.07, 87.07) * mm, "end": v(-80, 80) * mm});
            skLineSegment(sketch, "E79.2", {"start": v(-70, 90) * mm, "end": v(70, 90) * mm});
            skArc(sketch, "E79.3", {"start": v(80, 80) * mm, "mid": v(77.07, 87.07) * mm, "end": v(70, 90) * mm});
            skLineSegment(sketch, "E79.4", {"start": v(80, -80) * mm, "end": v(80, 80) * mm});
            skArc(sketch, "E79.5", {"start": v(70, -90) * mm, "mid": v(77.07, -87.07) * mm, "end": v(80, -80) * mm});
            skLineSegment(sketch, "E79.6", {"start": v(-70, -90) * mm, "end": v(70, -90) * mm});
            skArc(sketch, "E79.7", {"start": v(-80, -80) * mm, "mid": v(-77.07, -87.07) * mm, "end": v(-70, -90) * mm});
            skCircle(sketch, "E79.8", {"center": v(-60, -67.5) * mm, "radius": 4 * mm});
            skCircle(sketch, "E79.9", {"center": v(-60, 67.5) * mm, "radius": 4 * mm});
            skCircle(sketch, "E79.10", {"center": v(60, 67.5) * mm, "radius": 4 * mm});
            skCircle(sketch, "E79.11", {"center": v(60, -67.5) * mm, "radius": 4 * mm});
            skArc(sketch, "E79.12", {"start": v(-56.15, -48.18) * mm, "mid": v(0, -67.5) * mm, "end": v(56.15, -48.18) * mm});
            skLineSegment(sketch, "E79.13", {"start": v(60, 40.3) * mm, "end": v(60, -40.3) * mm});
            skArc(sketch, "E79.14", {"start": v(56.15, -48.18) * mm, "mid": v(58.99, -44.68) * mm, "end": v(60, -40.3) * mm});
            skArc(sketch, "E79.15", {"start": v(60, 40.3) * mm, "mid": v(58.99, 44.68) * mm, "end": v(56.15, 48.18) * mm});
            skArc(sketch, "E79.16", {"start": v(56.15, 48.18) * mm, "mid": v(0, 67.5) * mm, "end": v(-56.15, 48.18) * mm});
            skLineSegment(sketch, "E79.17", {"start": v(-60, 40.3) * mm, "end": v(-60, -40.3) * mm});
            skArc(sketch, "E79.18", {"start": v(-56.15, 48.18) * mm, "mid": v(-58.99, 44.68) * mm, "end": v(-60, 40.3) * mm});
            skArc(sketch, "E79.19", {"start": v(-60, -40.3) * mm, "mid": v(-58.99, -44.68) * mm, "end": v(-56.15, -48.18) * mm});
            skLineSegment(sketch, "E80", {"start": v(0, 90) * mm, "end": v(0, 120) * mm, "construction": true});
            skPoint(sketch, "E80.endSnap0", {"position": v(0, 90) * mm});
            skLineSegment(sketch, "E81", {"start": v(-33, 90) * mm, "end": v(-15, 108) * mm});
            skLineSegment(sketch, "E82", {"start": v(33, 90) * mm, "end": v(15, 108) * mm});
            skCircle(sketch, "E83", {"center": v(0, 120) * mm, "radius": 6 * mm});
            skLineSegment(sketch, "E84", {"start": v(-15, 108) * mm, "end": v(-15, 120) * mm});
            skLineSegment(sketch, "E85", {"start": v(15, 108) * mm, "end": v(15, 120) * mm});
            skArc(sketch, "E86", {"start": v(15, 120) * mm, "mid": v(0, 135) * mm, "end": v(-15, 120) * mm});
            skLineSegment(sketch, "E87", {"start": v(-80, 0) * mm, "end": v(80, 0) * mm, "construction": true});
            skLineSegment(sketch, "E88.MirrorCS", {"start": v(-33, -90) * mm, "end": v(-15, -108) * mm});
            skArc(sketch, "E89.MirrorCS", {"start": v(15, -120) * mm, "mid": v(0, -135) * mm, "end": v(-15, -120) * mm});
            skLineSegment(sketch, "E90.MirrorCS", {"start": v(33, -90) * mm, "end": v(15, -108) * mm});
            skCircle(sketch, "E91.MirrorC", {"center": v(0, -120) * mm, "radius": 6 * mm});
            skLineSegment(sketch, "E92.MirrorCS", {"start": v(0, -90) * mm, "end": v(0, -120) * mm, "construction": true});
            skLineSegment(sketch, "E93.MirrorCS", {"start": v(15, -108) * mm, "end": v(15, -120) * mm});
            skLineSegment(sketch, "E94.MirrorCS", {"start": v(-15, -108) * mm, "end": v(-15, -120) * mm});
            skSolve(sketch);
        }
        {
            var Q0;
            Q0 = qSketchRegion(id + "F16", true);
            extrude(context, id + "F17", {"entities" : qUnion([Q0]), "operationType" : NewBodyOperationType.ADD, "depth" : 25 * mm});
        }
    });
